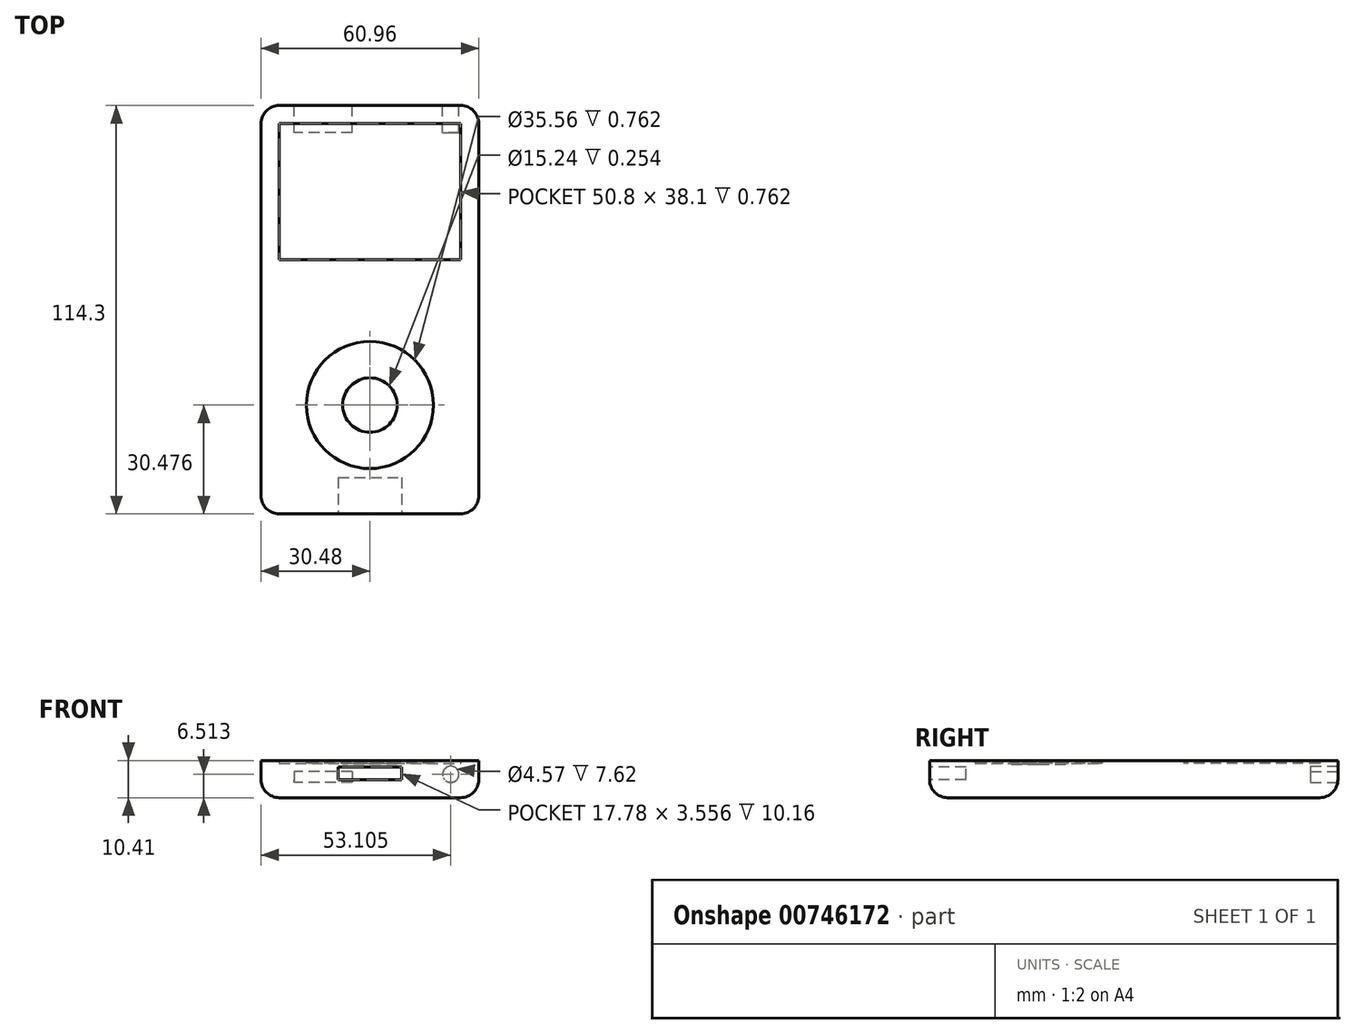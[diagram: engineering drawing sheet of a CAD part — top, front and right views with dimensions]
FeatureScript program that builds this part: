
annotation { "Feature Type Name" : "Feature", "Feature Type Description" : "" }
export const myFeature = defineFeature(function(context is Context, id is Id, definition is map)
    precondition{}
    {
        {
            var Q0;
            Q0=qCreatedBy(makeId("Top.planeOp"),FACE);
            var sketch = newSketch(context, id + "F0", { "sketchPlane" : qUnion([Q0])});
            skLineSegment(sketch, "E0.bottom", {"start": v(-25.4, 65.5) * mm, "end": v(25.4, 65.5) * mm});
            skLineSegment(sketch, "E0.top", {"start": v(-25.4, -48.8) * mm, "end": v(25.4, -48.8) * mm});
            skLineSegment(sketch, "E0.left", {"start": v(-30.48, 60.42) * mm, "end": v(-30.48, -43.72) * mm});
            skLineSegment(sketch, "E0.right", {"start": v(30.48, 60.42) * mm, "end": v(30.48, -43.72) * mm});
            skCircle(sketch, "E1", {"center": v(0, -18.32) * mm, "radius": 7.62 * mm});
            skCircle(sketch, "E2", {"center": v(0, -18.32) * mm, "radius": 17.78 * mm});
            skLineSegment(sketch, "E3.bottom", {"start": v(-25.4, 60.42) * mm, "end": v(25.4, 60.42) * mm});
            skLineSegment(sketch, "E3.top", {"start": v(-25.4, 22.32) * mm, "end": v(25.4, 22.32) * mm});
            skLineSegment(sketch, "E3.left", {"start": v(-25.4, 60.42) * mm, "end": v(-25.4, 22.32) * mm});
            skLineSegment(sketch, "E3.right", {"start": v(25.4, 60.42) * mm, "end": v(25.4, 22.32) * mm});
            skPoint(sketch, "E4.visualSharp", {"position": v(-30.48, 65.5) * mm});
            skArc(sketch, "E4.filletArc", {"start": v(-25.4, 65.5) * mm, "mid": v(-29, 64) * mm, "end": v(-30.48, 60.42) * mm});
            skPoint(sketch, "E5.visualSharp", {"position": v(30.48, 65.5) * mm});
            skArc(sketch, "E5.filletArc", {"start": v(30.48, 60.42) * mm, "mid": v(29, 64) * mm, "end": v(25.4, 65.5) * mm});
            skPoint(sketch, "E6.visualSharp", {"position": v(30.48, -48.8) * mm});
            skArc(sketch, "E6.filletArc", {"start": v(25.4, -48.8) * mm, "mid": v(29, -47.32) * mm, "end": v(30.48, -43.72) * mm});
            skPoint(sketch, "E7.visualSharp", {"position": v(-30.48, -48.8) * mm});
            skArc(sketch, "E7.filletArc", {"start": v(-30.48, -43.72) * mm, "mid": v(-29, -47.32) * mm, "end": v(-25.4, -48.8) * mm});
            skSolve(sketch);
        }
        {
            var Q0;
            Q0=makeQuery(id+"F0.imprint","IMPRINT",FACE,{"disambiguationData":[TD([[makeQuery(id+"F0.imprint","IMPRINT",EDGE,{"derivedFrom":sQuery(id+"F0.wireOp",EDGE,"E0.bottom")}),-1.0]])]});
            extrude(context, id + "F1", {"entities" : qUnion([Q0]), "depth" : 10.4 * mm, "offsetDistance" : 25.4 * mm});
        }
        {
            var Q0;
            Q0=makeQuery(id+"F1.opExtrude","CAP_EDGE",EDGE,{"disambiguationData":[OSD([sQuery(id+"F0.wireOp",EDGE,"E4.filletArc")])],"isStart":true});
            fillet(context, id + "F2", {"entities" : qUnion([Q0]), "radius" : 5.08 * mm, "tangentPropagation" : true, "allowEdgeOverflow" : false});
        }
        {
            var Q0;
            Q0=makeQuery(id+"F0.imprint","IMPRINT",FACE,{"disambiguationData":[TD([[makeQuery(id+"F0.imprint","IMPRINT",EDGE,{"derivedFrom":sQuery(id+"F0.wireOp",EDGE,"E3.bottom")}),-1.0]])]});
            extrude(context, id + "F3", {"entities" : qUnion([Q0]), "operationType" : NewBodyOperationType.ADD, "depth" : 9.65 * mm, "offsetDistance" : 25.4 * mm});
        }
        {
            var Q0;
            Q0=makeQuery(id+"F0.imprint","IMPRINT",FACE,{"disambiguationData":[TD([[makeQuery(id+"F0.imprint","IMPRINT",EDGE,{"derivedFrom":sQuery(id+"F0.wireOp",EDGE,"E1")}),-1.0]])]});
            extrude(context, id + "F4", {"entities" : qUnion([Q0]), "operationType" : NewBodyOperationType.ADD, "depth" : 9.65 * mm, "offsetDistance" : 25.4 * mm});
        }
        {
            var Q0;
            Q0=makeQuery(id+"F0.imprint","IMPRINT",FACE,{"disambiguationData":[TD([[makeQuery(id+"F0.imprint","IMPRINT",EDGE,{"derivedFrom":sQuery(id+"F0.wireOp",EDGE,"E1")}),1.0]])]});
            extrude(context, id + "F5", {"entities" : qUnion([Q0]), "operationType" : NewBodyOperationType.ADD, "depth" : 9.4 * mm, "offsetDistance" : 25.4 * mm});
        }
        {
            var Q0;
            Q0=makeQuery(id+"F1.opExtrude","SWEPT_FACE",FACE,{"disambiguationData":[OSD([sQuery(id+"F0.wireOp",EDGE,"E0.top")])]});
            var sketch = newSketch(context, id + "F6", { "sketchPlane" : qUnion([Q0])});
            skLineSegment(sketch, "E8.bottom", {"start": v(8.89, 5.08) * mm, "end": v(-8.9, 5.08) * mm});
            skLineSegment(sketch, "E8.top", {"start": v(8.89, 8.64) * mm, "end": v(-8.9, 8.64) * mm});
            skLineSegment(sketch, "E8.left", {"start": v(8.89, 5.08) * mm, "end": v(8.89, 8.64) * mm});
            skLineSegment(sketch, "E8.right", {"start": v(-8.9, 5.08) * mm, "end": v(-8.9, 8.64) * mm});
            skPoint(sketch, "E8.middle", {"position": v(0, 6.86) * mm});
            skPoint(sketch, "E8.middle.positionSnap0", {"position": v(0, 5.08) * mm});
            skPoint(sketch, "E8.centerSnap0", {"position": v(0, 5.08) * mm});
            skSolve(sketch);
        }
        {
            var Q0;
            Q0=makeQuery(id+"F6.imprint","IMPRINT",FACE,{"disambiguationData":[TD([[makeQuery(id+"F6.imprint","IMPRINT",EDGE,{"derivedFrom":sQuery(id+"F6.wireOp",EDGE,"E8.bottom")}),1.0]])]});
            extrude(context, id + "F7", {"entities" : qUnion([Q0]), "operationType" : NewBodyOperationType.REMOVE, "oppositeDirection" : true, "depth" : 10.16 * mm, "offsetDistance" : 25.4 * mm});
        }
        {
            var Q0;
            Q0=makeQuery(id+"F1.opExtrude","SWEPT_FACE",FACE,{"disambiguationData":[OSD([sQuery(id+"F0.wireOp",EDGE,"E0.bottom")])]});
            var sketch = newSketch(context, id + "F8", { "sketchPlane" : qUnion([Q0])});
            skCircle(sketch, "E9", {"center": v(-22.63, 6.51) * mm, "radius": 2.29 * mm});
            skLineSegment(sketch, "E10.bottom", {"start": v(4.97, 7.37) * mm, "end": v(21.2, 7.37) * mm});
            skLineSegment(sketch, "E10.top", {"start": v(4.97, 4.32) * mm, "end": v(21.2, 4.32) * mm});
            skLineSegment(sketch, "E10.left", {"start": v(4.97, 7.37) * mm, "end": v(4.97, 4.32) * mm});
            skLineSegment(sketch, "E10.right", {"start": v(21.2, 7.37) * mm, "end": v(21.2, 4.32) * mm});
            skSolve(sketch);
        }
        {
            var Q0;
            {var subQ0=sQuery(id+"F8.wireOp",EDGE,"E9");var subQ1=sQuery(id+"F0.wireOp",EDGE,"E0.bottom");var subQ2=makeQuery(id+"F2.opFillet","BLEND_EDGE",EDGE,{"blendedFrom":[makeQuery(id+"F1.opExtrude","CAP_EDGE",EDGE,{"disambiguationData":[OSD([subQ1])],"isStart":true}),makeQuery(id+"F1.opExtrude","SWEPT_FACE",FACE,{"disambiguationData":[OSD([subQ1])]})],"blendedInto":[makeQuery(id+"F1.opExtrude","SWEPT_FACE",FACE,{"disambiguationData":[OSD([subQ1])]})]});var subQ3=makeQuery(id+"F8.imprint","INTERSECT",VERTEX,{"disambiguationData":[OD(0.0)],"derivedFrom":[subQ2,subQ0]});Q0=makeQuery(id+"F8.imprint","IMPRINT",FACE,{"disambiguationData":[TD([[makeQuery(id+"F8.imprint","IMPRINT",EDGE,{"disambiguationData":[TD([[subQ3,1.0]])],"derivedFrom":subQ0}),1.0]])]});}
            var Q1;
            {var subQ0=sQuery(id+"F8.wireOp",EDGE,"E9");var subQ1=sQuery(id+"F0.wireOp",EDGE,"E0.bottom");var subQ2=makeQuery(id+"F2.opFillet","BLEND_EDGE",EDGE,{"blendedFrom":[makeQuery(id+"F1.opExtrude","CAP_EDGE",EDGE,{"disambiguationData":[OSD([subQ1])],"isStart":true}),makeQuery(id+"F1.opExtrude","SWEPT_FACE",FACE,{"disambiguationData":[OSD([subQ1])]})],"blendedInto":[makeQuery(id+"F1.opExtrude","SWEPT_FACE",FACE,{"disambiguationData":[OSD([subQ1])]})]});var subQ3=makeQuery(id+"F8.imprint","INTERSECT",VERTEX,{"disambiguationData":[OD(0.0)],"derivedFrom":[subQ2,subQ0]});Q1=makeQuery(id+"F8.imprint","IMPRINT",FACE,{"disambiguationData":[TD([[makeQuery(id+"F8.imprint","IMPRINT",EDGE,{"disambiguationData":[TD([[subQ3,-1.0]])],"derivedFrom":subQ0}),1.0]])]});}
            extrude(context, id + "F9", {"entities" : qUnion([Q0, Q1]), "operationType" : NewBodyOperationType.REMOVE, "oppositeDirection" : true, "depth" : 7.62 * mm, "offsetDistance" : 25.4 * mm});
        }
        {
            var Q0;
            {var subQ0=sQuery(id+"F8.wireOp",EDGE,"E10.bottom");Q0=makeQuery(id+"F8.imprint","IMPRINT",FACE,{"disambiguationData":[TD([[makeQuery(id+"F8.imprint","IMPRINT",EDGE,{"derivedFrom":subQ0}),-1.0]])]});}
            var Q1;
            {var subQ0=sQuery(id+"F8.wireOp",EDGE,"E10.top");Q1=makeQuery(id+"F8.imprint","IMPRINT",FACE,{"disambiguationData":[TD([[makeQuery(id+"F8.imprint","IMPRINT",EDGE,{"derivedFrom":subQ0}),1.0]])]});}
            extrude(context, id + "F10", {"entities" : qUnion([Q0, Q1]), "operationType" : NewBodyOperationType.REMOVE, "oppositeDirection" : true, "depth" : 7.62 * mm, "offsetDistance" : 25.4 * mm});
        }
    });
